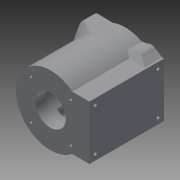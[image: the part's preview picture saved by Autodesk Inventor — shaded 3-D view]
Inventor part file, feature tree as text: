
AUTODESK INVENTOR PART (.ipt)
format: ipt  version: 2014 SP2 (Build 180246200, 246)  size: 345,088 bytes
history: native  units: mm
features: extrude x12, sketch x12, chamfer x6
ambient origin geometry x8: Origin, YZ Plane, XZ Plane, XY Plane, X Axis, Y Axis, Z Axis, Center Point
bodies: Solid1 (feature_tree)
feature tree (30):
  extrude  "Extrusion1"  Depth=52.0mm
  extrude  "Extrusion2"  Depth=3.0mm
  extrude  "Extrusion3"  Depth=3.0mm
  extrude  "Extrusion4"  Depth=10.0mm TaperAngle=0.0deg
  extrude  "Extrusion5"  Depth=59.0mm TaperAngle=0.0deg
  extrude  "Extrusion6"  Depth=14.0mm
  extrude  "Extrusion7"  Depth=14.0mm
  extrude  "Extrusion8"  Depth=28.0mm
  extrude  "Extrusion9"  Depth=30.0mm
  extrude  "Extrusion10"  Depth=14.0mm
  chamfer  "Chamfer1"  Distance=51.0mm
  chamfer  "Chamfer2"  Distance=14.0mm
  chamfer  "Chamfer3"  [1 undecoded]
  chamfer  "Chamfer4"  Distance=36.0mm
  extrude  "Extrusion11"  Depth=50.0mm
  chamfer  "Chamfer5"  Distance=25.0mm
  chamfer  "Chamfer6"  Distance=69.0mm
  extrude  "Extrusion12"  Depth=50.0mm
  sketch  "Sketch1"  dims[d0=28.0mm d1=52.0mm]
  sketch  "Sketch2"  dims[d2=64.0mm d3=3.0mm]
  sketch  "Sketch3"  dims[d4=3.0mm d5=3.0mm]
  sketch  "Sketch5"  dims[d6=3.0mm d7=10.0mm d8=0.0mm]
  sketch  "Sketch6"  dims[d9=37.0mm d10=59.0mm d11=0.0mm]
  sketch  "Sketch7"  dims[d12=30.0mm d13=14.0mm]
  sketch  "Sketch8"  dims[d14=15.0mm d15=14.0mm]
  sketch  "Sketch9"  dims[d22=8.0mm d26=28.0mm]
  sketch  "Sketch10"  dims[d27=8.0mm d28=30.0mm]
  sketch  "Sketch11"  dims[d29=3.384776mm d30=14.0mm d32=51.0mm d33=0.0mm]
  sketch  "Sketch12"  dims[d35=15.0mm]
  sketch  "Sketch13"  dims[d38=14.0mm d39=14.0mm d40=0.0mm d41=36.0mm d42=50.0mm d43=25.0mm d44=69.0mm d45=0.0mm d46=5.5mm d47=5.5mm d48=5.5mm d49=5.5mm d50=3.0mm d51=3.0mm d52=3.0mm d53=3.0mm d54=12.0mm d55=0.0mm d56=48.5mm d57=48.5mm d58=24.25mm d59=24.25mm d60=4.0mm d61=4.0mm d62=4.0mm d63=4.0mm d64=12.0mm d65=12.0mm d66=12.0mm d67=12.0mm d68=10.0mm d69=0.0mm d70=1.0mm d71=0.0mm d72=1.0mm d73=0.0mm d74=1.0mm d75=0.0mm d76=1.0mm d77=0.0mm d78=5.24mm d79=2.0mm d80=45.0deg d81=5.24mm d82=2.0mm d83=45.0deg d84=8.29mm d85=2.0mm d86=45.0deg d87=8.29mm d88=2.0mm d89=45.0deg d90=10.0mm d91=0.0mm d92=8.0mm d93=2.0mm d94=45.0deg d95=4.0mm d96=2.0mm d97=45.0deg d98=50.0mm d99=0.0mm]
note: 1 required parameter value undecoded (feature->parameter linkage not recoverable at this tier; creation-order binding heuristic only, values carry confidence <= 0.55)
